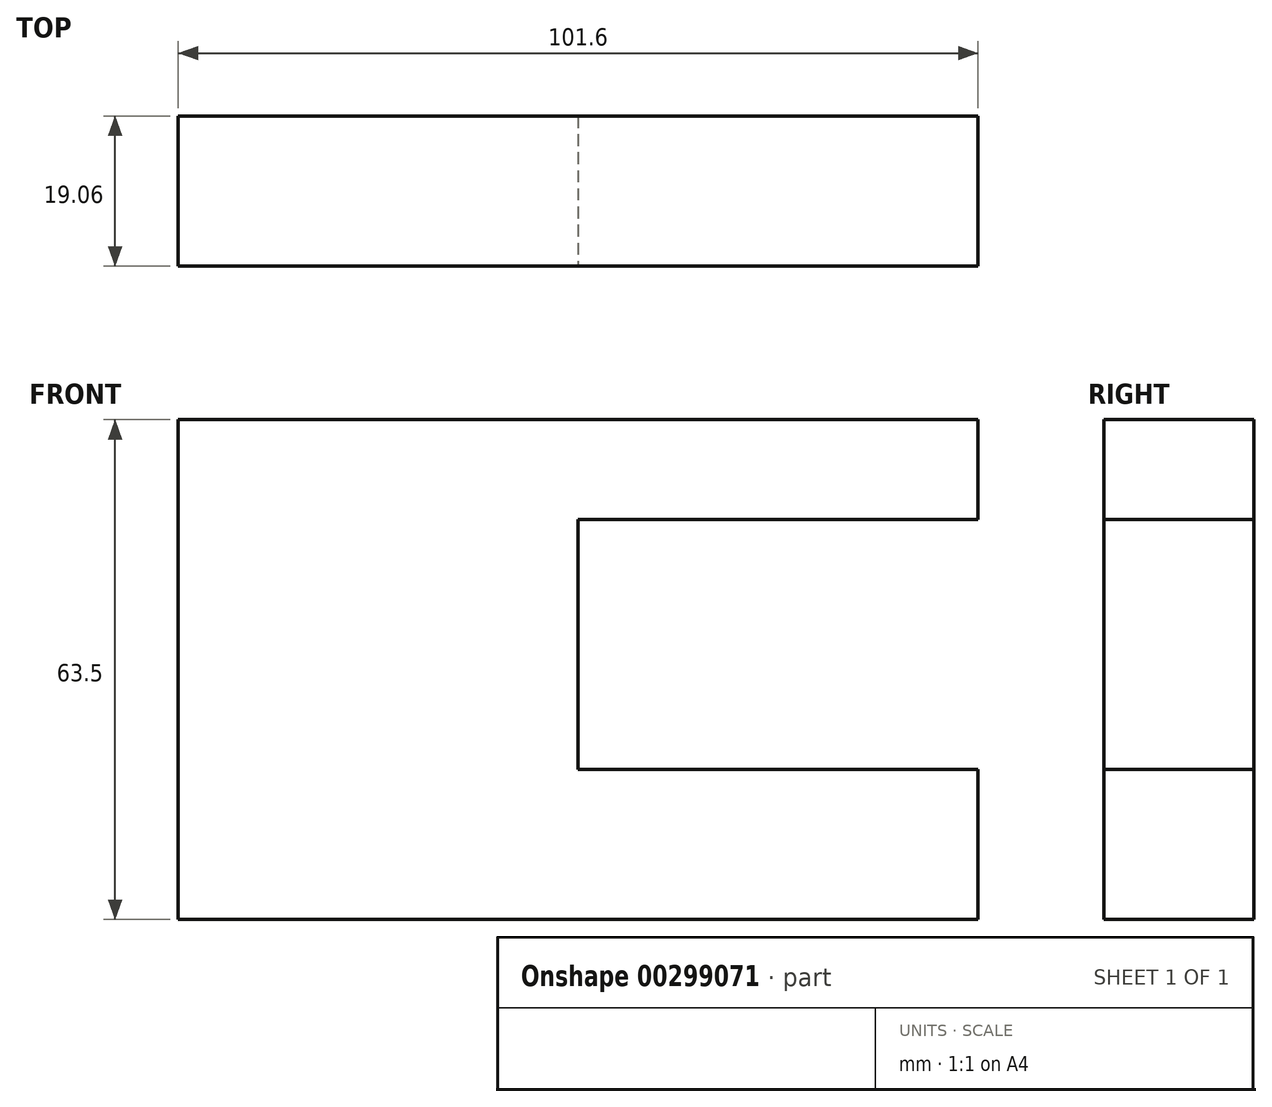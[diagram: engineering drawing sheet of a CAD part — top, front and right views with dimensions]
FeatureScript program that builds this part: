
annotation { "Feature Type Name" : "Feature", "Feature Type Description" : "" }
export const myFeature = defineFeature(function(context is Context, id is Id, definition is map)
    precondition{}
    {
        {
            var Q0;
            Q0=qCreatedBy(makeId("Top.planeOp"),FACE);
            var sketch = newSketch(context, id + "F0", { "sketchPlane" : qUnion([Q0])});
            skLineSegment(sketch, "E0.bottom", {"start": v(-50.8, 9.53) * mm, "end": v(50.8, 9.53) * mm});
            skLineSegment(sketch, "E0.top", {"start": v(-50.8, -9.53) * mm, "end": v(50.8, -9.53) * mm});
            skLineSegment(sketch, "E0.left", {"start": v(-50.8, 9.53) * mm, "end": v(-50.8, -9.52) * mm});
            skLineSegment(sketch, "E0.right", {"start": v(50.8, 9.53) * mm, "end": v(50.8, -9.52) * mm});
            skPoint(sketch, "E0.middle", {"position": v(0, 0) * mm});
            skLineSegment(sketch, "E1.bottom", {"start": v(-50.8, -9.53) * mm, "end": v(-25.4, -9.53) * mm});
            skLineSegment(sketch, "E1.top", {"start": v(-50.8, -28.58) * mm, "end": v(-25.4, -28.57) * mm});
            skLineSegment(sketch, "E1.left", {"start": v(-50.8, -9.53) * mm, "end": v(-50.8, -28.58) * mm});
            skLineSegment(sketch, "E1.right", {"start": v(-25.4, -9.52) * mm, "end": v(-25.4, -28.57) * mm});
            skSolve(sketch);
        }
        {
            var Q0;
            Q0=makeQuery(id+"F0.imprint","IMPRINT",FACE,{"disambiguationData":[TD([[makeQuery(id+"F0.imprint","IMPRINT",EDGE,{"derivedFrom":sQuery(id+"F0.wireOp",EDGE,"E0.bottom")}),-1.0]])]});
            var Q1;
            Q1=makeQuery(id+"F0.imprint","IMPRINT",FACE,{"disambiguationData":[TD([[makeQuery(id+"F0.imprint","IMPRINT",EDGE,{"derivedFrom":sQuery(id+"F0.wireOp",EDGE,"E1.bottom")}),-1.0]])]});
            extrude(context, id + "F1", {"entities" : qUnion([Q0, Q1]), "oppositeDirection" : true, "depth" : 63.5 * mm});
        }
        {
            var Q0;
            Q0=makeQuery(id+"F1.opExtrude","SWEPT_FACE",FACE,{"disambiguationData":[OSD([sQuery(id+"F0.wireOp",EDGE,"E0.top")])]});
            var sketch = newSketch(context, id + "F2", { "sketchPlane" : qUnion([Q0])});
            skLineSegment(sketch, "E2.bottom", {"start": v(50.8, -12.7) * mm, "end": v(0, -12.7) * mm});
            skLineSegment(sketch, "E2.top", {"start": v(50.8, -44.45) * mm, "end": v(0, -44.45) * mm});
            skLineSegment(sketch, "E2.left", {"start": v(50.8, -12.7) * mm, "end": v(50.8, -44.45) * mm});
            skLineSegment(sketch, "E2.right", {"start": v(0, -12.7) * mm, "end": v(0, -44.45) * mm});
            skSolve(sketch);
        }
        {
            var Q0;
            Q0 = qSketchRegion(id + "F2", true);
            extrude(context, id + "F3", {"entities" : qUnion([Q0]), "operationType" : NewBodyOperationType.REMOVE, "endBound" : BoundingType.THROUGH_ALL, "oppositeDirection" : true, "depth" : 25.4 * mm});
        }
    });
